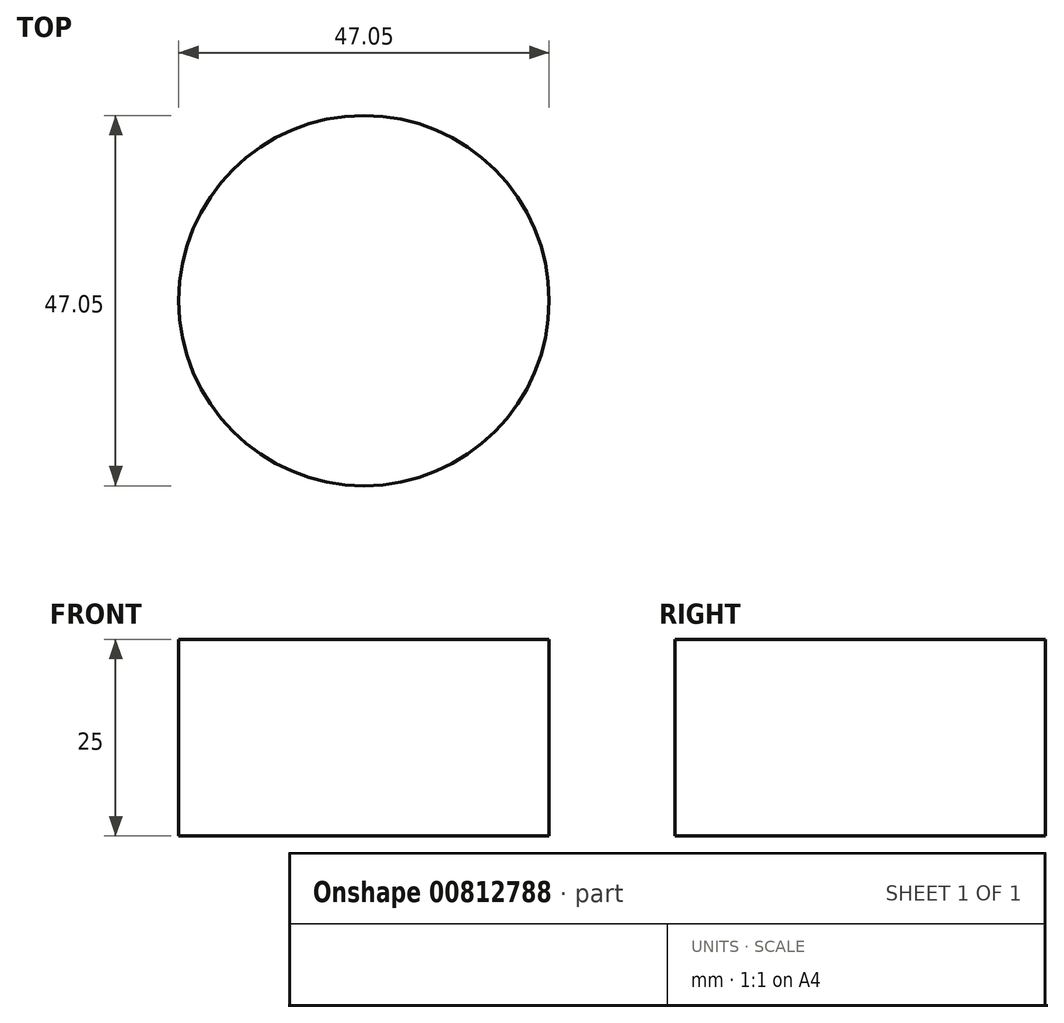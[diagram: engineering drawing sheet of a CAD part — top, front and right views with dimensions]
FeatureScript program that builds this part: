
annotation { "Feature Type Name" : "Feature", "Feature Type Description" : "" }
export const myFeature = defineFeature(function(context is Context, id is Id, definition is map)
    precondition{}
    {
        {
            var Q0;
            Q0=qCreatedBy(makeId("Top.planeOp"),FACE);
            var sketch = newSketch(context, id + "F0", { "sketchPlane" : qUnion([Q0])});
            skCircle(sketch, "E0", {"center": v(-60.28, -48.8) * mm, "radius": 23.53 * mm});
            skSolve(sketch);
        }
        {
            var Q0;
            Q0 = qSketchRegion(id + "F0", true);
            extrude(context, id + "F1", {"entities" : qUnion([Q0]), "depth" : 25 * mm, "offsetDistance" : 25 * mm});
        }
    });
